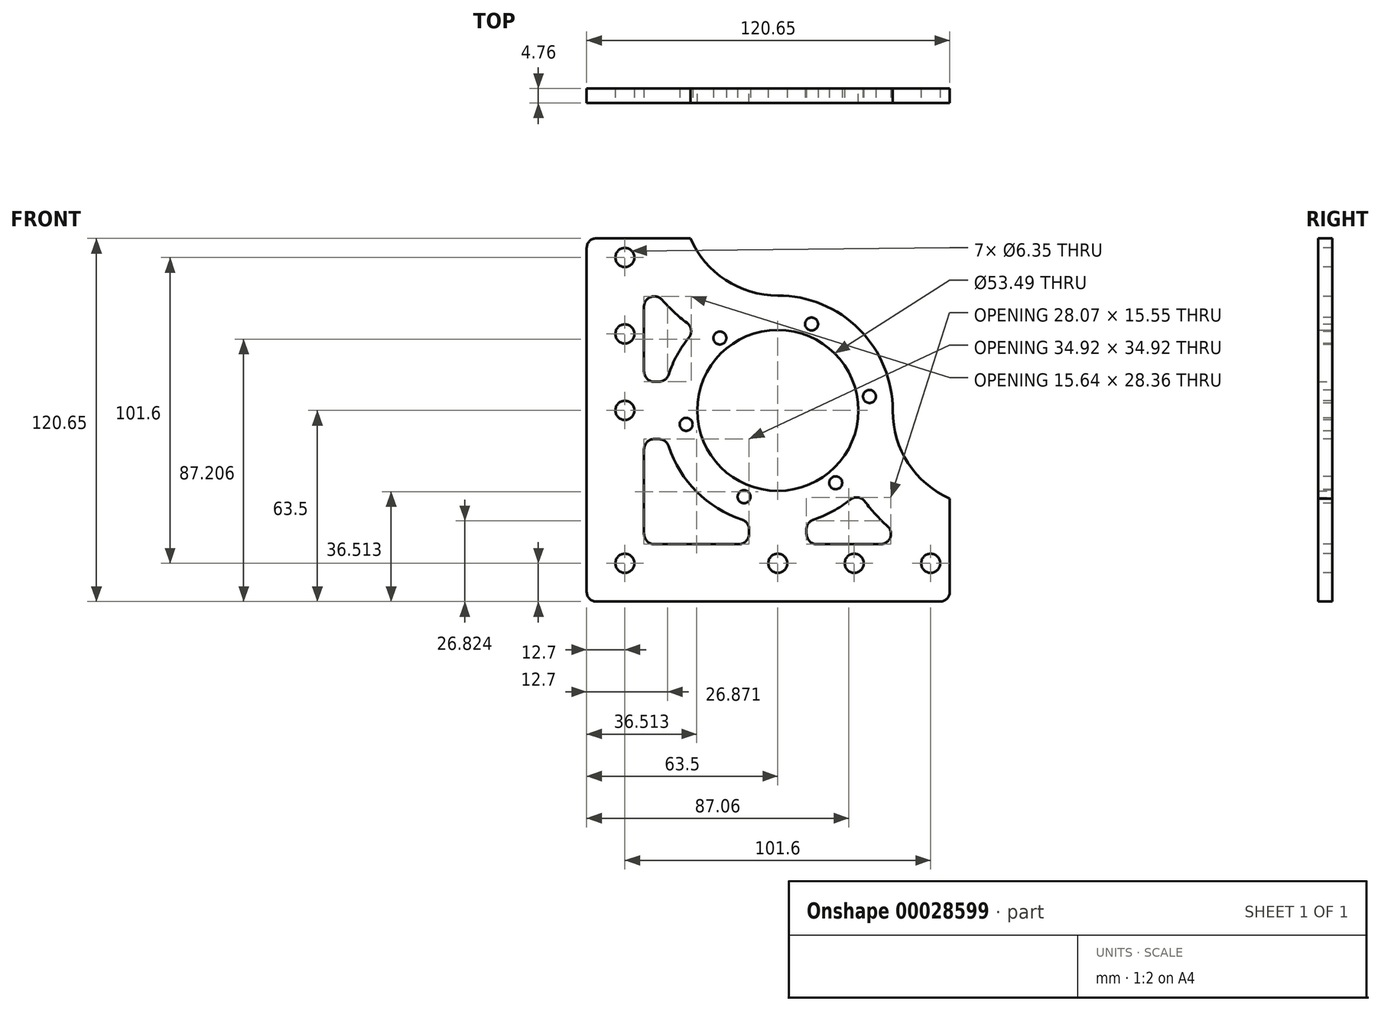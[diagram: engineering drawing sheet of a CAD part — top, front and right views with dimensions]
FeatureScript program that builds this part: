
annotation { "Feature Type Name" : "Feature", "Feature Type Description" : "" }
export const myFeature = defineFeature(function(context is Context, id is Id, definition is map)
    precondition{}
    {
        {
            var Q0;
            Q0=qCreatedBy(makeId("Front.planeOp"),FACE);
            var sketch = newSketch(context, id + "F0", { "sketchPlane" : qUnion([Q0])});
            skLineSegment(sketch, "E0.bottom", {"start": v(0, 0) * mm, "end": v(120.65, 0) * mm});
            skLineSegment(sketch, "E0.top", {"start": v(0, 120.65) * mm, "end": v(63.5, 120.65) * mm});
            skLineSegment(sketch, "E0.left", {"start": v(0, 0) * mm, "end": v(0, 120.65) * mm});
            skLineSegment(sketch, "E0.right", {"start": v(120.65, 0) * mm, "end": v(120.65, 120.65) * mm});
            skCircle(sketch, "E1", {"center": v(63.5, 63.5) * mm, "radius": 26.75 * mm});
            skCircle(sketch, "E2", {"center": v(63.5, 63.5) * mm, "radius": 38.18 * mm});
            skArc(sketch, "E3", {"start": v(34.44, 120.65) * mm, "mid": v(46.15, 106.84) * mm, "end": v(63.5, 101.68) * mm});
            skArc(sketch, "E4", {"start": v(101.68, 63.5) * mm, "mid": v(106.77, 46) * mm, "end": v(120.65, 34.19) * mm});
            skLineSegment(sketch, "E5", {"start": v(63.5, 63.5) * mm, "end": v(63.5, 186.08) * mm, "construction": true});
            skLineSegment(sketch, "E6", {"start": v(63.5, 63.5) * mm, "end": v(259.12, 63.5) * mm, "construction": true});
            skSolve(sketch);
        }
        {
            var Q0;
            Q0=makeQuery(id+"F0.imprint","IMPRINT",FACE,{"disambiguationData":[TD([[makeQuery(id+"F0.imprint","IMPRINT",EDGE,{"derivedFrom":sQuery(id+"F0.wireOp",EDGE,"E0.bottom")}),1.0]])]});
            var Q1;
            Q1=makeQuery(id+"F0.imprint","IMPRINT",FACE,{"disambiguationData":[TD([[makeQuery(id+"F0.imprint","IMPRINT",EDGE,{"derivedFrom":sQuery(id+"F0.wireOp",EDGE,"E1")}),-1.0]])]});
            extrude(context, id + "F1", {"entities" : qUnion([Q0, Q1]), "depth" : 4.76 * mm});
        }
        {
            var Q0;
            Q0=makeQuery(id+"F1.opExtrude","CAP_FACE",FACE,{"disambiguationData":[OSD([sQuery(id+"F0.wireOp",EDGE,"E0.bottom"),sQuery(id+"F0.wireOp",EDGE,"E0.top"),sQuery(id+"F0.wireOp",EDGE,"E0.left"),sQuery(id+"F0.wireOp",EDGE,"E0.right"),sQuery(id+"F0.wireOp",EDGE,"E1"),sQuery(id+"F0.wireOp",EDGE,"E2"),sQuery(id+"F0.wireOp",EDGE,"E3"),sQuery(id+"F0.wireOp",EDGE,"E4")])],"isStart":false});
            var sketch = newSketch(context, id + "F2", { "sketchPlane" : qUnion([Q0])});
            skLineSegment(sketch, "E7", {"start": v(63.5, 63.5) * mm, "end": v(63.5, 1.94) * mm, "construction": true});
            skLineSegment(sketch, "E8", {"start": v(63.5, 63.5) * mm, "end": v(3.21, 63.5) * mm, "construction": true});
            skLineSegment(sketch, "E9", {"start": v(53.98, 26.53) * mm, "end": v(53.98, 19.05) * mm});
            skLineSegment(sketch, "E10", {"start": v(73.03, 26.53) * mm, "end": v(73.03, 19.05) * mm});
            skLineSegment(sketch, "E11", {"start": v(26.53, 53.97) * mm, "end": v(19.05, 53.97) * mm});
            skLineSegment(sketch, "E12", {"start": v(26.53, 73.02) * mm, "end": v(19.05, 73.02) * mm});
            skLineSegment(sketch, "E13.0", {"start": v(19.05, 108.84) * mm, "end": v(19.05, 73.02) * mm});
            skArc(sketch, "E13.1", {"start": v(36.44, 90.43) * mm, "mid": v(26.58, 98.54) * mm, "end": v(19.05, 108.84) * mm});
            skArc(sketch, "E13.3", {"start": v(108.39, 19.05) * mm, "mid": v(98.28, 26.57) * mm, "end": v(90.34, 36.35) * mm});
            skLineSegment(sketch, "E13.4", {"start": v(19.05, 19.05) * mm, "end": v(53.98, 19.05) * mm});
            skArc(sketch, "E14", {"start": v(26.53, 53.98) * mm, "mid": v(36.5, 36.5) * mm, "end": v(53.98, 26.53) * mm});
            skLineSegment(sketch, "E15.trimOffspring", {"start": v(19.05, 53.97) * mm, "end": v(19.05, 19.05) * mm});
            skArc(sketch, "E16.trimOffspring", {"start": v(73.03, 26.53) * mm, "mid": v(82.33, 30.3) * mm, "end": v(90.34, 36.35) * mm});
            skLineSegment(sketch, "E17.trimOffspring", {"start": v(73.03, 19.05) * mm, "end": v(108.39, 19.05) * mm});
            skArc(sketch, "E18.trimOffspring", {"start": v(36.44, 90.43) * mm, "mid": v(30.33, 82.4) * mm, "end": v(26.53, 73.02) * mm});
            skSolve(sketch);
        }
        {
            var Q0;
            Q0=makeQuery(id+"F2.imprint","IMPRINT",FACE,{"disambiguationData":[TD([[makeQuery(id+"F2.imprint","IMPRINT",EDGE,{"derivedFrom":sQuery(id+"F2.wireOp",EDGE,"E12")}),-1.0]])]});
            var Q1;
            Q1=makeQuery(id+"F2.imprint","IMPRINT",FACE,{"disambiguationData":[TD([[makeQuery(id+"F2.imprint","IMPRINT",EDGE,{"derivedFrom":sQuery(id+"F2.wireOp",EDGE,"E9")}),-1.0]])]});
            var Q2;
            Q2=makeQuery(id+"F2.imprint","IMPRINT",FACE,{"disambiguationData":[TD([[makeQuery(id+"F2.imprint","IMPRINT",EDGE,{"derivedFrom":sQuery(id+"F2.wireOp",EDGE,"E10")}),1.0]])]});
            extrude(context, id + "F3", {"entities" : qUnion([Q0, Q1, Q2]), "operationType" : NewBodyOperationType.REMOVE, "oppositeDirection" : true, "depth" : 25.4 * mm});
        }
        {
            var Q0;
            Q0=makeQuery(id+"F3.boolean.opBoolean","COPY",EDGE,{"derivedFrom":makeQuery(id+"F3.opExtrude","SWEPT_EDGE",EDGE,{"disambiguationData":[OSD([sQuery(id+"F2.wireOp",EDGE,"E13.0"),sQuery(id+"F2.wireOp",EDGE,"E13.1")])]})});
            var Q1;
            Q1=makeQuery(id+"F3.boolean.opBoolean","COPY",EDGE,{"derivedFrom":makeQuery(id+"F3.opExtrude","SWEPT_EDGE",EDGE,{"disambiguationData":[OSD([sQuery(id+"F2.wireOp",EDGE,"E13.1"),sQuery(id+"F2.wireOp",EDGE,"E18.trimOffspring")])]})});
            var Q2;
            Q2=makeQuery(id+"F3.boolean.opBoolean","COPY",EDGE,{"derivedFrom":makeQuery(id+"F3.opExtrude","SWEPT_EDGE",EDGE,{"disambiguationData":[OSD([sQuery(id+"F2.wireOp",EDGE,"E12"),sQuery(id+"F2.wireOp",EDGE,"E13.0")])]})});
            var Q3;
            Q3=makeQuery(id+"F3.boolean.opBoolean","COPY",EDGE,{"derivedFrom":makeQuery(id+"F3.opExtrude","SWEPT_EDGE",EDGE,{"disambiguationData":[OSD([sQuery(id+"F2.wireOp",EDGE,"E12"),sQuery(id+"F2.wireOp",EDGE,"E18.trimOffspring")])]})});
            var Q4;
            Q4=makeQuery(id+"F3.boolean.opBoolean","COPY",EDGE,{"derivedFrom":makeQuery(id+"F3.opExtrude","SWEPT_EDGE",EDGE,{"disambiguationData":[OSD([sQuery(id+"F2.wireOp",EDGE,"E9"),sQuery(id+"F2.wireOp",EDGE,"E13.4")])]})});
            var Q5;
            Q5=makeQuery(id+"F3.boolean.opBoolean","COPY",EDGE,{"derivedFrom":makeQuery(id+"F3.opExtrude","SWEPT_EDGE",EDGE,{"disambiguationData":[OSD([sQuery(id+"F2.wireOp",EDGE,"E13.4"),sQuery(id+"F2.wireOp",EDGE,"E15.trimOffspring")])]})});
            var Q6;
            Q6=makeQuery(id+"F3.boolean.opBoolean","COPY",EDGE,{"derivedFrom":makeQuery(id+"F3.opExtrude","SWEPT_EDGE",EDGE,{"disambiguationData":[OSD([sQuery(id+"F2.wireOp",EDGE,"E11"),sQuery(id+"F2.wireOp",EDGE,"E15.trimOffspring")])]})});
            var Q7;
            Q7=makeQuery(id+"F3.boolean.opBoolean","COPY",EDGE,{"derivedFrom":makeQuery(id+"F3.opExtrude","SWEPT_EDGE",EDGE,{"disambiguationData":[OSD([sQuery(id+"F2.wireOp",EDGE,"E11"),sQuery(id+"F2.wireOp",EDGE,"E14")])]})});
            var Q8;
            Q8=makeQuery(id+"F3.boolean.opBoolean","COPY",EDGE,{"derivedFrom":makeQuery(id+"F3.opExtrude","SWEPT_EDGE",EDGE,{"disambiguationData":[OSD([sQuery(id+"F2.wireOp",EDGE,"E9"),sQuery(id+"F2.wireOp",EDGE,"E14")])]})});
            var Q9;
            Q9=makeQuery(id+"F3.boolean.opBoolean","COPY",EDGE,{"derivedFrom":makeQuery(id+"F3.opExtrude","SWEPT_EDGE",EDGE,{"disambiguationData":[OSD([sQuery(id+"F2.wireOp",EDGE,"E13.3"),sQuery(id+"F2.wireOp",EDGE,"E17.trimOffspring")])]})});
            var Q10;
            Q10=makeQuery(id+"F3.boolean.opBoolean","COPY",EDGE,{"derivedFrom":makeQuery(id+"F3.opExtrude","SWEPT_EDGE",EDGE,{"disambiguationData":[OSD([sQuery(id+"F2.wireOp",EDGE,"E13.3"),sQuery(id+"F2.wireOp",EDGE,"E16.trimOffspring")])]})});
            var Q11;
            Q11=makeQuery(id+"F3.boolean.opBoolean","COPY",EDGE,{"derivedFrom":makeQuery(id+"F3.opExtrude","SWEPT_EDGE",EDGE,{"disambiguationData":[OSD([sQuery(id+"F2.wireOp",EDGE,"E10"),sQuery(id+"F2.wireOp",EDGE,"E16.trimOffspring")])]})});
            var Q12;
            Q12=makeQuery(id+"F3.boolean.opBoolean","COPY",EDGE,{"derivedFrom":makeQuery(id+"F3.opExtrude","SWEPT_EDGE",EDGE,{"disambiguationData":[OSD([sQuery(id+"F2.wireOp",EDGE,"E10"),sQuery(id+"F2.wireOp",EDGE,"E17.trimOffspring")])]})});
            fillet(context, id + "F4", {"entities" : qUnion([Q0, Q1, Q2, Q3, Q4, Q5, Q6, Q7, Q8, Q9, Q10, Q11, Q12]), "radius" : 3.43 * mm, "tangentPropagation" : true, "allowEdgeOverflow" : false});
        }
        {
            var Q0;
            Q0=makeQuery(id+"F1.opExtrude","CAP_FACE",FACE,{"disambiguationData":[OSD([sQuery(id+"F0.wireOp",EDGE,"E0.bottom"),sQuery(id+"F0.wireOp",EDGE,"E0.top"),sQuery(id+"F0.wireOp",EDGE,"E0.left"),sQuery(id+"F0.wireOp",EDGE,"E0.right"),sQuery(id+"F0.wireOp",EDGE,"E1"),sQuery(id+"F0.wireOp",EDGE,"E2"),sQuery(id+"F0.wireOp",EDGE,"E3"),sQuery(id+"F0.wireOp",EDGE,"E4")])],"isStart":false});
            var sketch = newSketch(context, id + "F5", { "sketchPlane" : qUnion([Q0])});
            skLineSegment(sketch, "E19", {"start": v(-15.06, 12.7) * mm, "end": v(139.87, 12.7) * mm, "construction": true});
            skLineSegment(sketch, "E20", {"start": v(12.7, -17.42) * mm, "end": v(12.7, 136.04) * mm, "construction": true});
            skPoint(sketch, "E21", {"position": v(12.7, 114.3) * mm});
            skPoint(sketch, "E22", {"position": v(12.7, 88.9) * mm});
            skPoint(sketch, "E23", {"position": v(12.7, 63.5) * mm});
            skPoint(sketch, "E24", {"position": v(63.5, 12.7) * mm});
            skPoint(sketch, "E25", {"position": v(88.9, 12.7) * mm});
            skPoint(sketch, "E26", {"position": v(114.3, 12.7) * mm});
            skPoint(sketch, "E27", {"position": v(12.7, 12.7) * mm});
            skSolve(sketch);
        }
        {
            var Q0;
            Q0=sQuery(id+"F5.wireOp",VERTEX,"E27");
            var Q1;
            Q1=sQuery(id+"F5.wireOp",VERTEX,"E24");
            var Q2;
            Q2=sQuery(id+"F5.wireOp",VERTEX,"E25");
            var Q3;
            Q3=sQuery(id+"F5.wireOp",VERTEX,"E26");
            var Q4;
            Q4=sQuery(id+"F5.wireOp",VERTEX,"E23");
            var Q5;
            Q5=sQuery(id+"F5.wireOp",VERTEX,"E22");
            var Q6;
            Q6=sQuery(id+"F5.wireOp",VERTEX,"E21");
            var Q7;
            Q7=makeQuery(id+"F1.opExtrude","SWEPT_BODY",BODY,{"disambiguationData":[OSD([sQuery(id+"F0.wireOp",EDGE,"E0.bottom"),sQuery(id+"F0.wireOp",EDGE,"E0.top"),sQuery(id+"F0.wireOp",EDGE,"E0.left"),sQuery(id+"F0.wireOp",EDGE,"E0.right"),sQuery(id+"F0.wireOp",EDGE,"E1"),sQuery(id+"F0.wireOp",EDGE,"E2"),sQuery(id+"F0.wireOp",EDGE,"E3"),sQuery(id+"F0.wireOp",EDGE,"E4")])]});
            hole(context, id + "F6", {"style" : HoleStyle.SIMPLE, "holeDiameter" : 6.35 * mm, "endStyle" : HoleEndStyle.THROUGH, "locations" : qUnion([Q0, Q1, Q2, Q3, Q4, Q5, Q6]), "scope" : qUnion([Q7])});
        }
        {
            var Q0;
            Q0=makeQuery(id+"F1.opExtrude","CAP_FACE",FACE,{"disambiguationData":[OSD([sQuery(id+"F0.wireOp",EDGE,"E0.bottom"),sQuery(id+"F0.wireOp",EDGE,"E0.top"),sQuery(id+"F0.wireOp",EDGE,"E0.left"),sQuery(id+"F0.wireOp",EDGE,"E0.right"),sQuery(id+"F0.wireOp",EDGE,"E1"),sQuery(id+"F0.wireOp",EDGE,"E2"),sQuery(id+"F0.wireOp",EDGE,"E3"),sQuery(id+"F0.wireOp",EDGE,"E4")])],"isStart":false});
            var sketch = newSketch(context, id + "F7", { "sketchPlane" : qUnion([Q0])});
            skCircle(sketch, "E28.cCircle", {"center": v(63.5, 63.5) * mm, "radius": 30.8 * mm, "construction": true});
            skLineSegment(sketch, "E28.0", {"start": v(74.71, 92.2) * mm, "end": v(93.95, 68.14) * mm});
            skLineSegment(sketch, "E28.1", {"start": v(93.95, 68.14) * mm, "end": v(82.74, 39.45) * mm});
            skLineSegment(sketch, "E28.2", {"start": v(82.74, 39.45) * mm, "end": v(52.29, 34.8) * mm});
            skLineSegment(sketch, "E28.3", {"start": v(52.29, 34.8) * mm, "end": v(33.05, 58.86) * mm});
            skLineSegment(sketch, "E28.4", {"start": v(33.05, 58.86) * mm, "end": v(44.26, 87.55) * mm});
            skLineSegment(sketch, "E28.5", {"start": v(44.26, 87.55) * mm, "end": v(74.71, 92.2) * mm});
            skSolve(sketch);
        }
        {
            var Q0;
            Q0=sQuery(id+"F7.wireOp",VERTEX,"E28.0.start");
            var Q1;
            Q1=sQuery(id+"F7.wireOp",VERTEX,"E28.4.end");
            var Q2;
            Q2=sQuery(id+"F7.wireOp",VERTEX,"E28.3.end");
            var Q3;
            Q3=sQuery(id+"F7.wireOp",VERTEX,"E28.3.start");
            var Q4;
            Q4=sQuery(id+"F7.wireOp",VERTEX,"E28.2.start");
            var Q5;
            Q5=sQuery(id+"F7.wireOp",VERTEX,"E28.1.start");
            var Q6;
            Q6=makeQuery(id+"F1.opExtrude","SWEPT_BODY",BODY,{"disambiguationData":[OSD([sQuery(id+"F0.wireOp",EDGE,"E0.bottom"),sQuery(id+"F0.wireOp",EDGE,"E0.top"),sQuery(id+"F0.wireOp",EDGE,"E0.left"),sQuery(id+"F0.wireOp",EDGE,"E0.right"),sQuery(id+"F0.wireOp",EDGE,"E1"),sQuery(id+"F0.wireOp",EDGE,"E2"),sQuery(id+"F0.wireOp",EDGE,"E3"),sQuery(id+"F0.wireOp",EDGE,"E4")])]});
            hole(context, id + "F8", {"style" : HoleStyle.SIMPLE, "holeDiameter" : 4.3 * mm, "endStyle" : HoleEndStyle.THROUGH, "locations" : qUnion([Q0, Q1, Q2, Q3, Q4, Q5]), "scope" : qUnion([Q6])});
        }
        {
            var Q0;
            Q0=makeQuery(id+"F1.opExtrude","SWEPT_EDGE",EDGE,{"disambiguationData":[OSD([sQuery(id+"F0.wireOp",EDGE,"E0.top"),sQuery(id+"F0.wireOp",EDGE,"E0.left")])]});
            var Q1;
            Q1=makeQuery(id+"F1.opExtrude","SWEPT_EDGE",EDGE,{"disambiguationData":[OSD([sQuery(id+"F0.wireOp",EDGE,"E0.bottom"),sQuery(id+"F0.wireOp",EDGE,"E0.left")])]});
            var Q2;
            Q2=makeQuery(id+"F1.opExtrude","SWEPT_EDGE",EDGE,{"disambiguationData":[OSD([sQuery(id+"F0.wireOp",EDGE,"E0.bottom"),sQuery(id+"F0.wireOp",EDGE,"E0.right")])]});
            fillet(context, id + "F9", {"entities" : qUnion([Q0, Q1, Q2]), "radius" : 3.17 * mm, "tangentPropagation" : true, "allowEdgeOverflow" : false});
        }
    });
